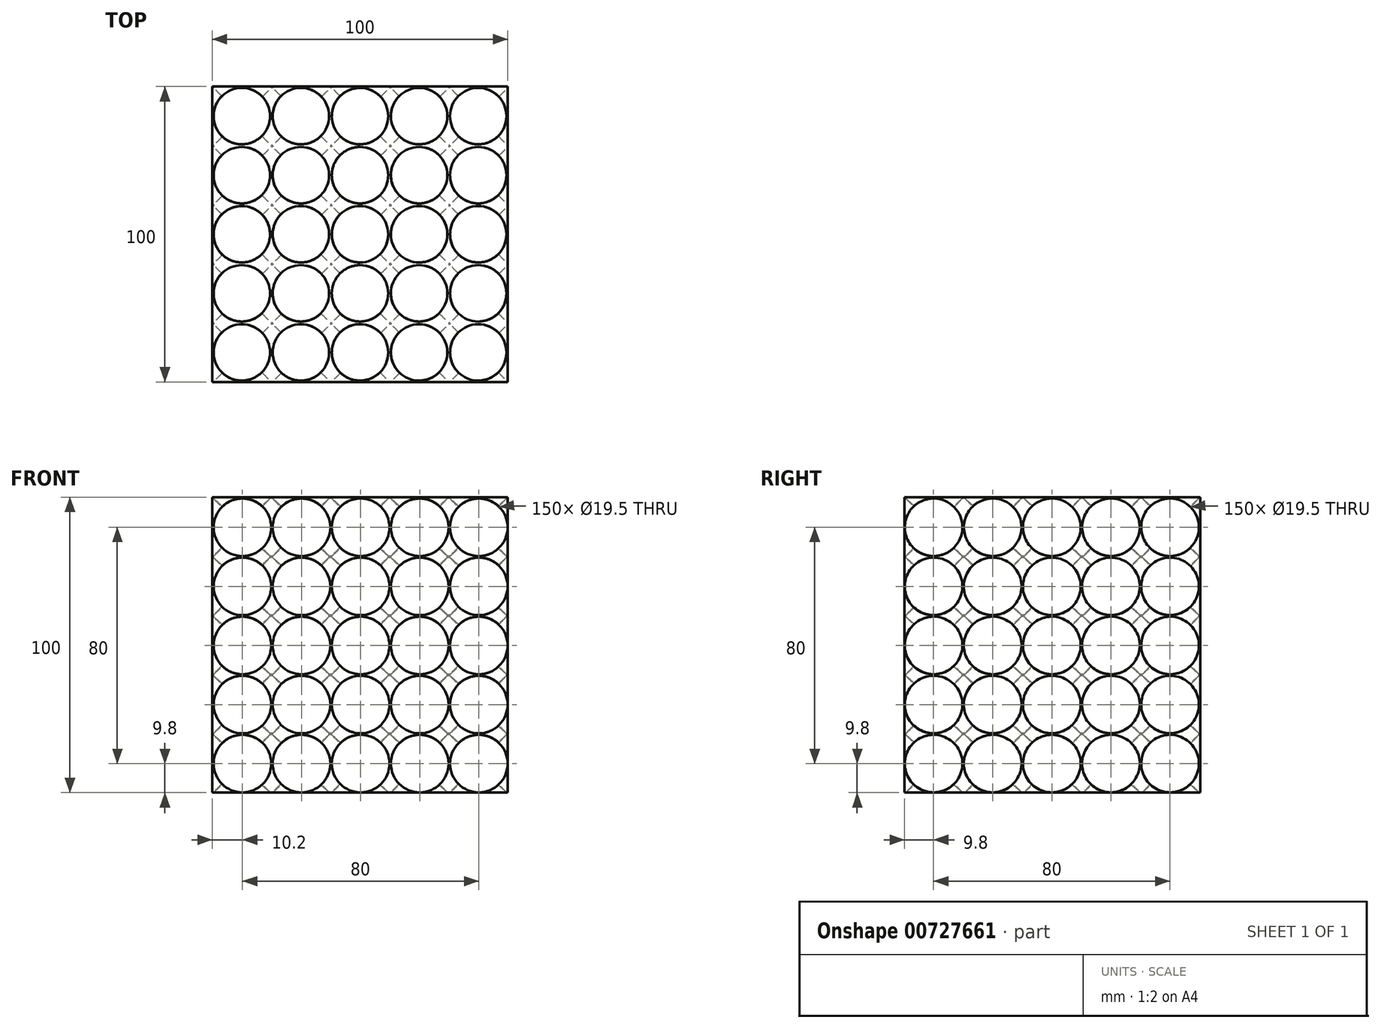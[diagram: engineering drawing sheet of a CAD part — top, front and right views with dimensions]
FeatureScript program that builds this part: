
annotation { "Feature Type Name" : "Feature", "Feature Type Description" : "" }
export const myFeature = defineFeature(function(context is Context, id is Id, definition is map)
    precondition{}
    {
        {
            var Q0;
            Q0=qCreatedBy(makeId("Top.planeOp"),FACE);
            var sketch = newSketch(context, id + "F0", { "sketchPlane" : qUnion([Q0])});
            skLineSegment(sketch, "E0.bottom", {"start": v(-50, 50) * mm, "end": v(50, 50) * mm});
            skLineSegment(sketch, "E0.top", {"start": v(-50, -50) * mm, "end": v(50, -50) * mm});
            skLineSegment(sketch, "E0.left", {"start": v(-50, 50) * mm, "end": v(-50, -50) * mm});
            skLineSegment(sketch, "E0.right", {"start": v(50, 50) * mm, "end": v(50, -50) * mm});
            skSolve(sketch);
        }
        {
            var Q0;
            Q0 = qSketchRegion(id + "F0", true);
            extrude(context, id + "F1", {"entities" : qUnion([Q0]), "endBound" : BoundingType.SYMMETRIC, "depth" : 100 * mm, "offsetDistance" : 25 * mm});
        }
        {
            var Q0;
            Q0=makeQuery(id+"F1.opExtrude","CAP_FACE",FACE,{"disambiguationData":[OSD([sQuery(id+"F0.wireOp",EDGE,"E0.bottom"),sQuery(id+"F0.wireOp",EDGE,"E0.top"),sQuery(id+"F0.wireOp",EDGE,"E0.left"),sQuery(id+"F0.wireOp",EDGE,"E0.right")])],"isStart":false});
            var sketch = newSketch(context, id + "F2", { "sketchPlane" : qUnion([Q0])});
            skCircle(sketch, "E1", {"center": v(-40, 40) * mm, "radius": 9.55 * mm});
            skLineSegment(sketch, "E2", {"start": v(-40, 40) * mm, "end": v(-50, 40) * mm, "construction": true});
            skLineSegment(sketch, "E3", {"start": v(-40, 50) * mm, "end": v(-40, 40) * mm, "construction": true});
            skCircle(sketch, "E4.0.1.0", {"center": v(-40, 20) * mm, "radius": 9.55 * mm});
            skCircle(sketch, "E4.0.2.0", {"center": v(-40, 0) * mm, "radius": 9.55 * mm});
            skCircle(sketch, "E4.0.3.0", {"center": v(-40, -20) * mm, "radius": 9.55 * mm});
            skCircle(sketch, "E4.0.4.0", {"center": v(-40, -40) * mm, "radius": 9.55 * mm});
            skCircle(sketch, "E4.1.0.0", {"center": v(-20, 40) * mm, "radius": 9.55 * mm});
            skCircle(sketch, "E4.1.1.0", {"center": v(-20, 20) * mm, "radius": 9.55 * mm});
            skCircle(sketch, "E4.1.2.0", {"center": v(-20, 0) * mm, "radius": 9.55 * mm});
            skCircle(sketch, "E4.1.3.0", {"center": v(-20, -20) * mm, "radius": 9.55 * mm});
            skCircle(sketch, "E4.1.4.0", {"center": v(-20, -40) * mm, "radius": 9.55 * mm});
            skCircle(sketch, "E4.2.0.0", {"center": v(0, 40) * mm, "radius": 9.55 * mm});
            skCircle(sketch, "E4.2.1.0", {"center": v(0, 20) * mm, "radius": 9.55 * mm});
            skCircle(sketch, "E4.2.2.0", {"center": v(0, 0) * mm, "radius": 9.55 * mm});
            skCircle(sketch, "E4.2.3.0", {"center": v(0, -20) * mm, "radius": 9.55 * mm});
            skCircle(sketch, "E4.2.4.0", {"center": v(0, -40) * mm, "radius": 9.55 * mm});
            skCircle(sketch, "E4.3.0.0", {"center": v(20, 40) * mm, "radius": 9.55 * mm});
            skCircle(sketch, "E4.3.1.0", {"center": v(20, 20) * mm, "radius": 9.55 * mm});
            skCircle(sketch, "E4.3.2.0", {"center": v(20, 0) * mm, "radius": 9.55 * mm});
            skCircle(sketch, "E4.3.3.0", {"center": v(20, -20) * mm, "radius": 9.55 * mm});
            skCircle(sketch, "E4.3.4.0", {"center": v(20, -40) * mm, "radius": 9.55 * mm});
            skCircle(sketch, "E4.4.0.0", {"center": v(40, 40) * mm, "radius": 9.55 * mm});
            skCircle(sketch, "E4.4.1.0", {"center": v(40, 20) * mm, "radius": 9.55 * mm});
            skCircle(sketch, "E4.4.2.0", {"center": v(40, 0) * mm, "radius": 9.55 * mm});
            skCircle(sketch, "E4.4.3.0", {"center": v(40, -20) * mm, "radius": 9.55 * mm});
            skCircle(sketch, "E4.4.4.0", {"center": v(40, -40) * mm, "radius": 9.55 * mm});
            skLineSegment(sketch, "E4.direction1", {"start": v(-40, 40) * mm, "end": v(-20, 40) * mm, "construction": true});
            skLineSegment(sketch, "E4.direction2", {"start": v(-40, 40) * mm, "end": v(-40, 20) * mm, "construction": true});
            skSolve(sketch);
        }
        {
            var Q0;
            Q0 = qSketchRegion(id + "F2", true);
            extrude(context, id + "F3", {"entities" : qUnion([Q0]), "operationType" : NewBodyOperationType.REMOVE, "endBound" : BoundingType.THROUGH_ALL, "oppositeDirection" : true, "depth" : 25 * mm, "offsetDistance" : 25 * mm});
        }
        {
            var Q0;
            Q0=makeQuery(id+"F1.opExtrude","SWEPT_FACE",FACE,{"disambiguationData":[OSD([sQuery(id+"F0.wireOp",EDGE,"E0.top")])]});
            var sketch = newSketch(context, id + "F4", { "sketchPlane" : qUnion([Q0])});
            skCircle(sketch, "E5", {"center": v(-39.8, 39.8) * mm, "radius": 9.75 * mm});
            skLineSegment(sketch, "E6", {"start": v(-39.8, 39.8) * mm, "end": v(-50, 39.8) * mm, "construction": true});
            skLineSegment(sketch, "E7", {"start": v(-39.8, 50) * mm, "end": v(-39.8, 39.8) * mm, "construction": true});
            skCircle(sketch, "E8.0.1.0", {"center": v(-39.8, 19.8) * mm, "radius": 9.75 * mm});
            skCircle(sketch, "E8.0.2.0", {"center": v(-39.8, -0.2) * mm, "radius": 9.75 * mm});
            skCircle(sketch, "E8.0.3.0", {"center": v(-39.8, -20.2) * mm, "radius": 9.75 * mm});
            skCircle(sketch, "E8.0.4.0", {"center": v(-39.8, -40.2) * mm, "radius": 9.75 * mm});
            skCircle(sketch, "E8.1.0.0", {"center": v(-19.8, 39.8) * mm, "radius": 9.75 * mm});
            skCircle(sketch, "E8.1.1.0", {"center": v(-19.8, 19.8) * mm, "radius": 9.75 * mm});
            skCircle(sketch, "E8.1.2.0", {"center": v(-19.8, -0.2) * mm, "radius": 9.75 * mm});
            skCircle(sketch, "E8.1.3.0", {"center": v(-19.8, -20.2) * mm, "radius": 9.75 * mm});
            skCircle(sketch, "E8.1.4.0", {"center": v(-19.8, -40.2) * mm, "radius": 9.75 * mm});
            skCircle(sketch, "E8.2.0.0", {"center": v(0.2, 39.8) * mm, "radius": 9.75 * mm});
            skCircle(sketch, "E8.2.1.0", {"center": v(0.2, 19.8) * mm, "radius": 9.75 * mm});
            skCircle(sketch, "E8.2.2.0", {"center": v(0.2, -0.2) * mm, "radius": 9.75 * mm});
            skCircle(sketch, "E8.2.3.0", {"center": v(0.2, -20.2) * mm, "radius": 9.75 * mm});
            skCircle(sketch, "E8.2.4.0", {"center": v(0.2, -40.2) * mm, "radius": 9.75 * mm});
            skCircle(sketch, "E8.3.0.0", {"center": v(20.2, 39.8) * mm, "radius": 9.75 * mm});
            skCircle(sketch, "E8.3.1.0", {"center": v(20.2, 19.8) * mm, "radius": 9.75 * mm});
            skCircle(sketch, "E8.3.2.0", {"center": v(20.2, -0.2) * mm, "radius": 9.75 * mm});
            skCircle(sketch, "E8.3.3.0", {"center": v(20.2, -20.2) * mm, "radius": 9.75 * mm});
            skCircle(sketch, "E8.3.4.0", {"center": v(20.2, -40.2) * mm, "radius": 9.75 * mm});
            skCircle(sketch, "E8.4.0.0", {"center": v(40.2, 39.8) * mm, "radius": 9.75 * mm});
            skCircle(sketch, "E8.4.1.0", {"center": v(40.2, 19.8) * mm, "radius": 9.75 * mm});
            skCircle(sketch, "E8.4.2.0", {"center": v(40.2, -0.2) * mm, "radius": 9.75 * mm});
            skCircle(sketch, "E8.4.3.0", {"center": v(40.2, -20.2) * mm, "radius": 9.75 * mm});
            skCircle(sketch, "E8.4.4.0", {"center": v(40.2, -40.2) * mm, "radius": 9.75 * mm});
            skLineSegment(sketch, "E8.direction1", {"start": v(-39.8, 39.8) * mm, "end": v(-19.8, 39.8) * mm, "construction": true});
            skLineSegment(sketch, "E8.direction2", {"start": v(-39.8, 39.8) * mm, "end": v(-39.8, 19.8) * mm, "construction": true});
            skSolve(sketch);
        }
        {
            var Q0;
            Q0 = qSketchRegion(id + "F4", true);
            extrude(context, id + "F5", {"entities" : qUnion([Q0]), "operationType" : NewBodyOperationType.REMOVE, "endBound" : BoundingType.THROUGH_ALL, "oppositeDirection" : true, "depth" : 25 * mm, "offsetDistance" : 25 * mm});
        }
        {
            var Q0;
            Q0=makeQuery(id+"F1.opExtrude","SWEPT_FACE",FACE,{"disambiguationData":[OSD([sQuery(id+"F0.wireOp",EDGE,"E0.left")])]});
            var sketch = newSketch(context, id + "F6", { "sketchPlane" : qUnion([Q0])});
            skCircle(sketch, "E9", {"center": v(-39.8, 39.8) * mm, "radius": 9.75 * mm});
            skLineSegment(sketch, "E10", {"start": v(-39.8, 39.8) * mm, "end": v(-50, 39.8) * mm, "construction": true});
            skLineSegment(sketch, "E11", {"start": v(-39.8, 50) * mm, "end": v(-39.8, 39.8) * mm, "construction": true});
            skCircle(sketch, "E12.0.1.0", {"center": v(-39.8, 19.8) * mm, "radius": 9.75 * mm});
            skCircle(sketch, "E12.0.2.0", {"center": v(-39.8, -0.2) * mm, "radius": 9.75 * mm});
            skCircle(sketch, "E12.0.3.0", {"center": v(-39.8, -20.2) * mm, "radius": 9.75 * mm});
            skCircle(sketch, "E12.0.4.0", {"center": v(-39.8, -40.2) * mm, "radius": 9.75 * mm});
            skCircle(sketch, "E12.1.0.0", {"center": v(-19.8, 39.8) * mm, "radius": 9.75 * mm});
            skCircle(sketch, "E12.1.1.0", {"center": v(-19.8, 19.8) * mm, "radius": 9.75 * mm});
            skCircle(sketch, "E12.1.2.0", {"center": v(-19.8, -0.2) * mm, "radius": 9.75 * mm});
            skCircle(sketch, "E12.1.3.0", {"center": v(-19.8, -20.2) * mm, "radius": 9.75 * mm});
            skCircle(sketch, "E12.1.4.0", {"center": v(-19.8, -40.2) * mm, "radius": 9.75 * mm});
            skCircle(sketch, "E12.2.0.0", {"center": v(0.2, 39.8) * mm, "radius": 9.75 * mm});
            skCircle(sketch, "E12.2.1.0", {"center": v(0.2, 19.8) * mm, "radius": 9.75 * mm});
            skCircle(sketch, "E12.2.2.0", {"center": v(0.2, -0.2) * mm, "radius": 9.75 * mm});
            skCircle(sketch, "E12.2.3.0", {"center": v(0.2, -20.2) * mm, "radius": 9.75 * mm});
            skCircle(sketch, "E12.2.4.0", {"center": v(0.2, -40.2) * mm, "radius": 9.75 * mm});
            skCircle(sketch, "E12.3.0.0", {"center": v(20.2, 39.8) * mm, "radius": 9.75 * mm});
            skCircle(sketch, "E12.3.1.0", {"center": v(20.2, 19.8) * mm, "radius": 9.75 * mm});
            skCircle(sketch, "E12.3.2.0", {"center": v(20.2, -0.2) * mm, "radius": 9.75 * mm});
            skCircle(sketch, "E12.3.3.0", {"center": v(20.2, -20.2) * mm, "radius": 9.75 * mm});
            skCircle(sketch, "E12.3.4.0", {"center": v(20.2, -40.2) * mm, "radius": 9.75 * mm});
            skCircle(sketch, "E12.4.0.0", {"center": v(40.2, 39.8) * mm, "radius": 9.75 * mm});
            skCircle(sketch, "E12.4.1.0", {"center": v(40.2, 19.8) * mm, "radius": 9.75 * mm});
            skCircle(sketch, "E12.4.2.0", {"center": v(40.2, -0.2) * mm, "radius": 9.75 * mm});
            skCircle(sketch, "E12.4.3.0", {"center": v(40.2, -20.2) * mm, "radius": 9.75 * mm});
            skCircle(sketch, "E12.4.4.0", {"center": v(40.2, -40.2) * mm, "radius": 9.75 * mm});
            skLineSegment(sketch, "E12.direction1", {"start": v(-39.8, 39.8) * mm, "end": v(-19.8, 39.8) * mm, "construction": true});
            skLineSegment(sketch, "E12.direction2", {"start": v(-39.8, 39.8) * mm, "end": v(-39.8, 19.8) * mm, "construction": true});
            skSolve(sketch);
        }
        {
            var Q0;
            Q0 = qSketchRegion(id + "F6", true);
            extrude(context, id + "F7", {"entities" : qUnion([Q0]), "operationType" : NewBodyOperationType.REMOVE, "endBound" : BoundingType.THROUGH_ALL, "oppositeDirection" : true, "depth" : 25 * mm, "offsetDistance" : 25 * mm});
        }
    });
